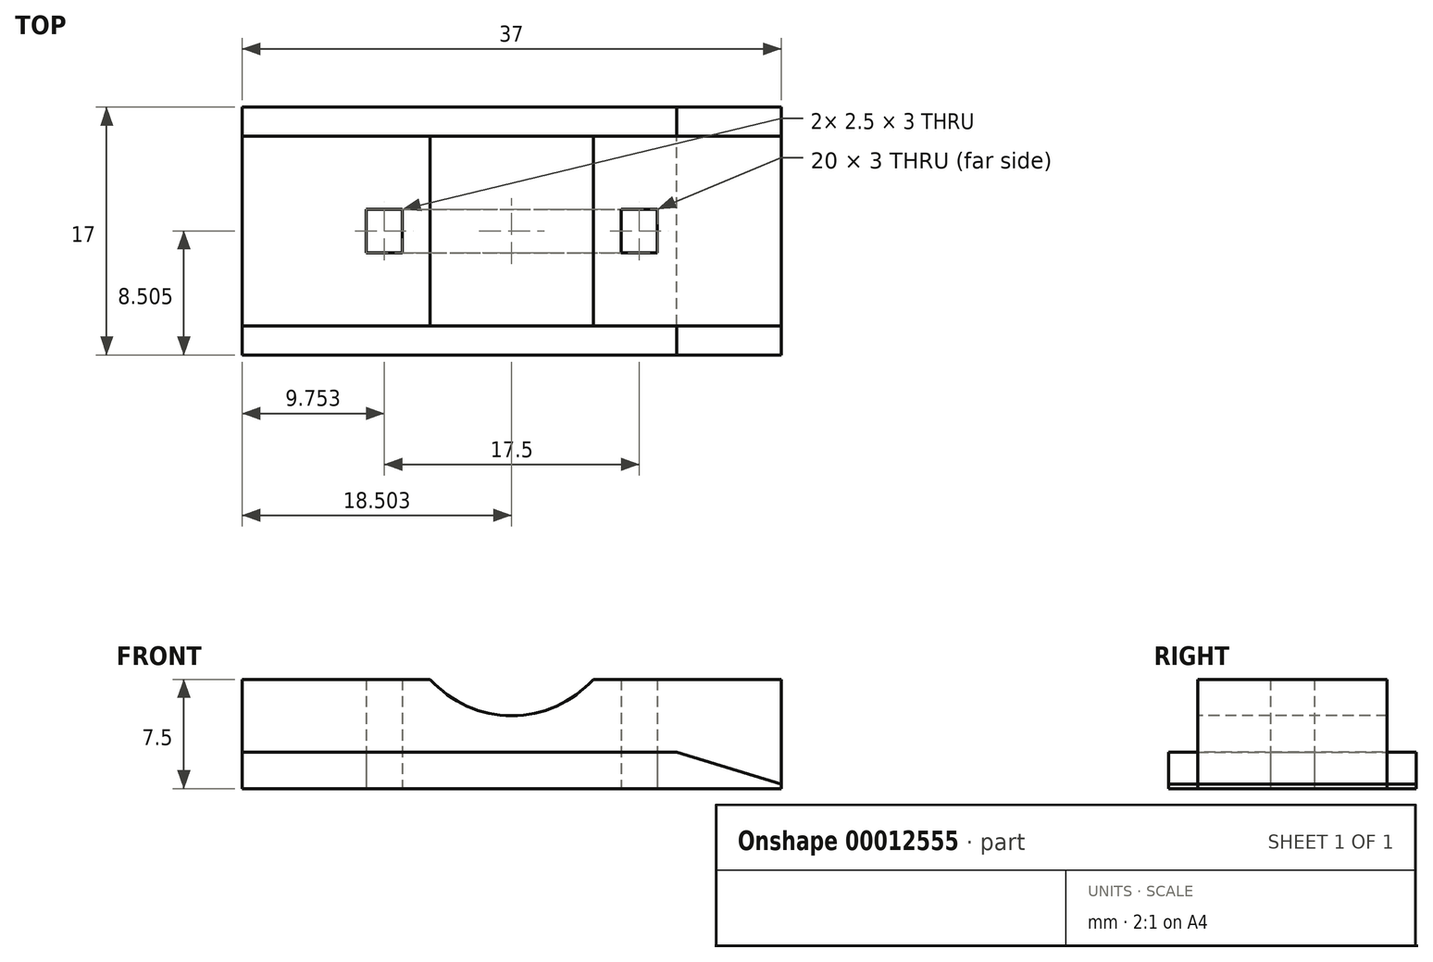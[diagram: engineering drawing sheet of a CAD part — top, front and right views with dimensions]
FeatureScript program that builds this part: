
annotation { "Feature Type Name" : "Feature", "Feature Type Description" : "" }
export const myFeature = defineFeature(function(context is Context, id is Id, definition is map)
    precondition{}
    {
        {
            var Q0;
            Q0=qCreatedBy(makeId("Top.planeOp"),FACE);
            var sketch = newSketch(context, id + "F0", { "sketchPlane" : qUnion([Q0])});
            skLineSegment(sketch, "E0.bottom", {"start": v(-17.23, 7.85) * mm, "end": v(19.77, 7.85) * mm});
            skLineSegment(sketch, "E1", {"start": v(-17.23, 5.85) * mm, "end": v(19.77, 5.85) * mm});
            skLineSegment(sketch, "E2", {"start": v(-17.23, 7.85) * mm, "end": v(-17.23, -0.65) * mm});
            skLineSegment(sketch, "E3", {"start": v(19.77, 7.85) * mm, "end": v(19.77, -0.65) * mm});
            skLineSegment(sketch, "E4", {"start": v(-17.23, -0.65) * mm, "end": v(19.77, -0.65) * mm});
            skLineSegment(sketch, "E5.0.MirrorCS", {"start": v(-17.23, -9.15) * mm, "end": v(-17.23, -0.65) * mm});
            skLineSegment(sketch, "E6.0.MirrorCS", {"start": v(-17.23, -7.15) * mm, "end": v(19.77, -7.15) * mm});
            skLineSegment(sketch, "E7.0.MirrorCS", {"start": v(-17.23, -9.15) * mm, "end": v(19.77, -9.15) * mm});
            skLineSegment(sketch, "E8.0.MirrorCS", {"start": v(19.77, -9.15) * mm, "end": v(19.77, -0.65) * mm});
            skLineSegment(sketch, "E9", {"start": v(-8.73, -0.65) * mm, "end": v(-8.73, 0.85) * mm});
            skLineSegment(sketch, "E10", {"start": v(-8.73, 0.85) * mm, "end": v(11.27, 0.85) * mm});
            skLineSegment(sketch, "E11", {"start": v(11.27, 0.85) * mm, "end": v(11.27, -0.65) * mm});
            skLineSegment(sketch, "E12", {"start": v(-6.23, 0.85) * mm, "end": v(-6.23, -0.65) * mm});
            skLineSegment(sketch, "E13", {"start": v(8.77, 0.85) * mm, "end": v(8.77, -0.65) * mm});
            skLineSegment(sketch, "E14.0.MirrorCS", {"start": v(-8.73, -0.65) * mm, "end": v(-8.73, -2.15) * mm});
            skLineSegment(sketch, "E15.0.MirrorCS", {"start": v(-8.73, -2.15) * mm, "end": v(11.27, -2.15) * mm});
            skLineSegment(sketch, "E16.0.MirrorCS", {"start": v(-6.23, -2.15) * mm, "end": v(-6.23, -0.65) * mm});
            skLineSegment(sketch, "E17.0.MirrorCS", {"start": v(8.77, -2.15) * mm, "end": v(8.77, -0.65) * mm});
            skLineSegment(sketch, "E18.0.MirrorCS", {"start": v(11.27, -2.15) * mm, "end": v(11.27, -0.65) * mm});
            skSolve(sketch);
        }
        {
            var Q0;
            {var subQ1=sQuery(id+"F0.wireOp",EDGE,"E1");Q0=makeQuery(id+"F0.imprint","IMPRINT",FACE,{"disambiguationData":[TD([[makeQuery(id+"F0.imprint","IMPRINT",EDGE,{"derivedFrom":subQ1}),1.0]])]});}
            var Q1;
            {var subQ2=sQuery(id+"F0.wireOp",EDGE,"E1");Q1=makeQuery(id+"F0.imprint","IMPRINT",FACE,{"disambiguationData":[TD([[makeQuery(id+"F0.imprint","IMPRINT",EDGE,{"derivedFrom":subQ2}),-1.0]])]});}
            var Q2;
            {var subQ2=sQuery(id+"F0.wireOp",EDGE,"E4");Q2=makeQuery(id+"F0.imprint","IMPRINT",FACE,{"disambiguationData":[TD([[makeQuery(id+"F0.imprint","IMPRINT",EDGE,{"derivedFrom":subQ2}),-1.0]])]});}
            var Q3;
            {var subQ3=sQuery(id+"F0.wireOp",EDGE,"E6.0.MirrorCS");Q3=makeQuery(id+"F0.imprint","IMPRINT",FACE,{"disambiguationData":[TD([[makeQuery(id+"F0.imprint","IMPRINT",EDGE,{"derivedFrom":subQ3}),-1.0]])]});}
            extrude(context, id + "F1", {"entities" : qUnion([Q0, Q1, Q2, Q3]), "depth" : 2.5 * mm});
        }
        {
            var Q0;
            {var subQ2=sQuery(id+"F0.wireOp",EDGE,"E4");Q0=makeQuery(id+"F0.imprint","IMPRINT",FACE,{"disambiguationData":[TD([[makeQuery(id+"F0.imprint","IMPRINT",EDGE,{"derivedFrom":subQ2}),-1.0]])]});}
            var Q1;
            {var subQ2=sQuery(id+"F0.wireOp",EDGE,"E1");Q1=makeQuery(id+"F0.imprint","IMPRINT",FACE,{"disambiguationData":[TD([[makeQuery(id+"F0.imprint","IMPRINT",EDGE,{"derivedFrom":subQ2}),-1.0]])]});}
            var Q2;
            {var subQ1=sQuery(id+"F0.wireOp",EDGE,"E16.0.MirrorCS");Q2=makeQuery(id+"F0.imprint","IMPRINT",FACE,{"disambiguationData":[TD([[makeQuery(id+"F0.imprint","IMPRINT",EDGE,{"derivedFrom":subQ1}),-1.0]])]});}
            var Q3;
            {var subQ2=sQuery(id+"F0.wireOp",EDGE,"E12");Q3=makeQuery(id+"F0.imprint","IMPRINT",FACE,{"disambiguationData":[TD([[makeQuery(id+"F0.imprint","IMPRINT",EDGE,{"derivedFrom":subQ2}),1.0]])]});}
            extrude(context, id + "F2", {"entities" : qUnion([Q0, Q1, Q2, Q3]), "depth" : 7.5 * mm});
        }
        {
            var Q0;
            Q0=makeQuery(id+"F2.opExtrude","SWEPT_FACE",FACE,{"disambiguationData":[OSD([sQuery(id+"F0.wireOp",EDGE,"E6.0.MirrorCS")])]});
            var sketch = newSketch(context, id + "F3", { "sketchPlane" : qUnion([Q0])});
            skCircle(sketch, "E19", {"center": v(1.27, 12.5) * mm, "radius": 7.5 * mm});
            skSolve(sketch);
        }
        {
            var Q0;
            {var subQ0=makeQuery(id+"F2.opExtrude","CAP_EDGE",EDGE,{"disambiguationData":[OSD([sQuery(id+"F0.wireOp",EDGE,"E6.0.MirrorCS")])],"isStart":false});var subQ1=sQuery(id+"F3.wireOp",EDGE,"E19");var subQ3=makeQuery(id+"F3.imprint","INTERSECT",VERTEX,{"disambiguationData":[OD(0.0)],"derivedFrom":[subQ0,subQ1]});Q0=makeQuery(id+"F3.imprint","IMPRINT",FACE,{"disambiguationData":[TD([[makeQuery(id+"F3.imprint","IMPRINT",EDGE,{"disambiguationData":[TD([[subQ3,-1.0]])],"derivedFrom":subQ1}),1.0]])]});}
            extrude(context, id + "F4", {"entities" : qUnion([Q0]), "operationType" : NewBodyOperationType.REMOVE, "oppositeDirection" : true, "depth" : 15 * mm});
        }
        {
            var Q0;
            Q0=makeQuery(id+"F1.opExtrude","CAP_EDGE",EDGE,{"disambiguationData":[OSD([sQuery(id+"F0.wireOp",EDGE,"E3"),sQuery(id+"F0.wireOp",EDGE,"E8.0.MirrorCS")])],"isStart":false});
            chamfer(context, id + "F5", {"entities" : qUnion([Q0]), "chamferType" : ChamferType.OFFSET_ANGLE, "width" : 2.2 * mm, "oppositeDirection" : false, "angle" : 73 * degree, "tangentPropagation" : true});
        }
    });
